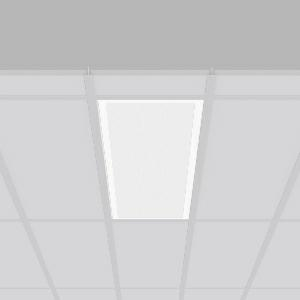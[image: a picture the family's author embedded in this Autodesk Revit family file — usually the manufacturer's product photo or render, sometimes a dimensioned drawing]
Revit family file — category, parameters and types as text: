
# Revit family: sidelite_eco_312368_002_1_790_5b45
name_source: partatom
category: Lighting Fixtures
units: mm (PartAtom-declared; Revit-internal decimal feet)

## family parameters
Cut with Voids When Loaded = No
Host = Face
Light Source = No
Part Type = Normal
Room Calculation Point = No
Round Connector Dimension = Use Diameter
Shared = No

## types (1)
- MultiLumen 1 (1 x LED Modul 840, 3500 lm, 4000)
    Apparent Load = 29 VA
    CIE Flux Codes = 64 88 97 100 100
    Color Rendering = 80
    Color Temperature = 4000
    Default Elevation = 1800 mm
    Description = Series: SIDELITE ECO
Highly economical recessed luminaire with progressive LED technology. Frame made of aluminium, powder-coated. Diffuser plastic microprismatic. Lightguide and diffuser made of non-yellowing plastic (PMMA). Lateral light emission (RZB SIDELITE technology) for homogeneous light distribution. External driver. External driver with simple plug-in locking system and extended converter connecting cable to luminaire (1.90 m). MultiLumen: 4 steps adjustable luminous flux. Factory setting is the lowest offered step. Luminaire can be used with accessories (to be ordered separately) as recessed or surface mounting luminaire. Perfect for office areas (RUG < 19) and environments with computer screens in accordance with EN 12464-1. Qualified for use in the food and drink industry. 
Colour: white
Length: 1245 mm
Width: 308 mm
Cut-out length: 1233 mm
Cut-out width: 296 mm
Recess height: 160 mm
Luminaire: recess height: 37 mm
Lamp: LED
Socket: without socket
Colour temperature: 4000K
Colour rendering index (CRI): 80
System power: 29 W
Rated luminous flux: 3500 lm
Luminous efficiency: 121 lm/W
System power 2: 33 W
Rated luminous flux 2: 3850 lm
Luminous efficiency 2: 117 lm/W
System power 3: 35 W
Rated luminous flux 3: 4050 lm
Luminous efficiency 3: 116 lm/W
System power 4: 38 W
Rated luminous flux 4: 4400 lm
Luminous efficiency 4: 116 lm/W
Control gear: Regulated power supply
Protection class: II
Type of protection: IP 40
    Height = 0 mm  [stored 0 ft]
    Lamp = 1 x LED Modul 840
    Lamp Light Flux = 3500 lm
    Lamp count = 1
    Length = 1245 mm
    Lifetime = 50000 h
    Luminous efficacy = 121 lm/W
    Manufacturer = RZB
    ModVariant = No
    Model = 312368.002.1.790
    Mounting Place = Ceiling
    Mounting Type = Recessed
    Number of Poles = 1
    OnlyDefault = Yes
    Power Factor = 1
    Product Name = SIDELITE ECO
    Product group = Recessed modular luminaires
    ProductGroupID = 406
    Protection Class = Protection class II
    Protection Degree = IP 20
    RLX_Detail_Level = 1
    RLX_Emergency_Light_Flux = 0 lm
    RLX_Emergency_Type = 0
    RLX_Emergency_Type_DB = No
    RlxData = <blob elided: 36073 chars, md5=0a164235>
    Socket = socket
    Standby Power = 0 W
    System Light Flux = 3500 lm
    System Power = 29 W
    Type Comments = MultiLumen 1
    Type Image = 312368.002.jpg
    URL = http://relux.com
    VarID = multilumen_1
    Voltage = 230 V
    Voltage Range = 220-240 V
    Weight = 0.00 kg
    Width = 308 mm

note: [stored X ft] marks values corroborated as IEEE doubles in the binary element streams (Revit-internal decimal feet)

## geometry (parser evidence)
native form markers: Blend x4, Sweep x9
no freeform markers — native parametric forms only
